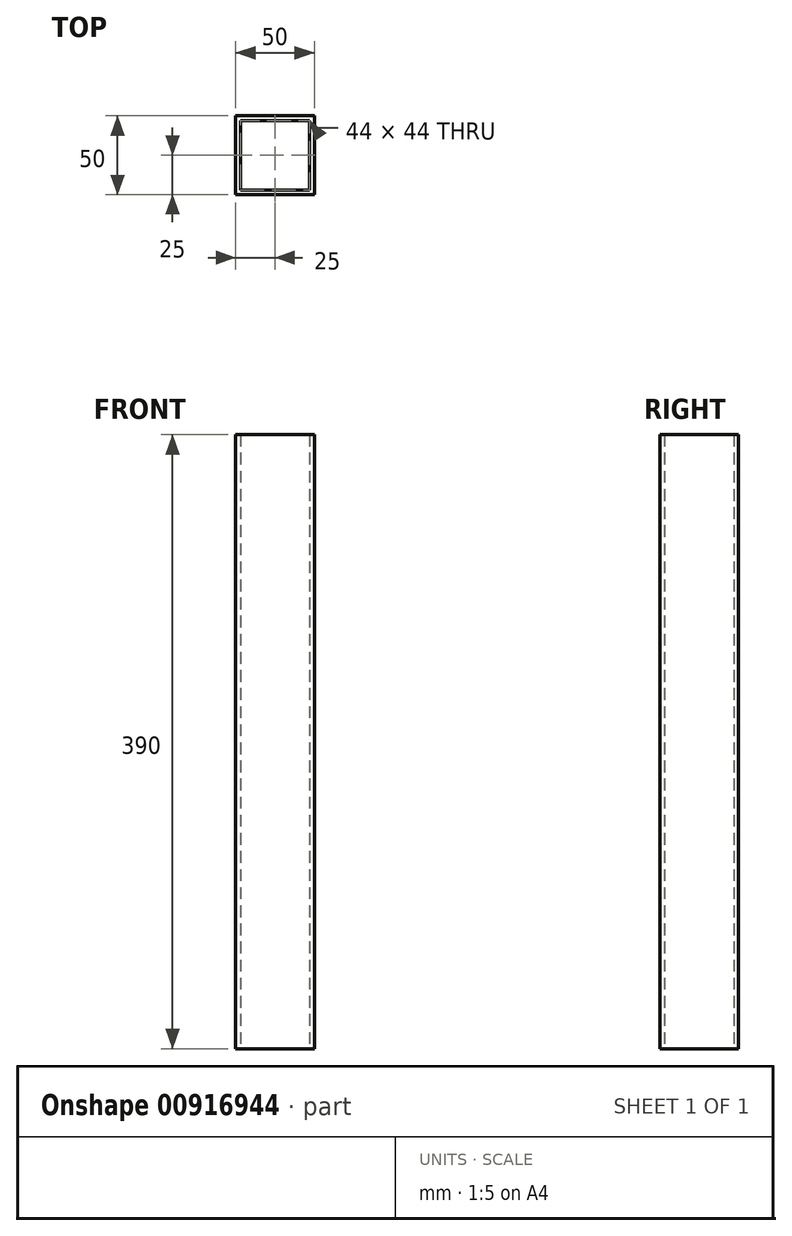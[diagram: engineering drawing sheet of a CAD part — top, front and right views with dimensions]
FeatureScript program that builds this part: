
annotation { "Feature Type Name" : "Feature", "Feature Type Description" : "" }
export const myFeature = defineFeature(function(context is Context, id is Id, definition is map)
    precondition{}
    {
        {
            var Q0;
            Q0=qCreatedBy(makeId("Top.planeOp"),FACE);
            var sketch = newSketch(context, id + "F0", { "sketchPlane" : qUnion([Q0])});
            skLineSegment(sketch, "E0.bottom", {"start": v(0, 0) * mm, "end": v(50, 0) * mm});
            skLineSegment(sketch, "E0.top", {"start": v(0, 50) * mm, "end": v(50, 50) * mm});
            skLineSegment(sketch, "E0.left", {"start": v(0, 0) * mm, "end": v(0, 50) * mm});
            skLineSegment(sketch, "E0.right", {"start": v(50, 0) * mm, "end": v(50, 50) * mm});
            skLineSegment(sketch, "E1.0", {"start": v(3, 3) * mm, "end": v(47, 3) * mm});
            skLineSegment(sketch, "E1.1", {"start": v(3, 3) * mm, "end": v(3, 47) * mm});
            skLineSegment(sketch, "E1.2", {"start": v(3, 47) * mm, "end": v(47, 47) * mm});
            skLineSegment(sketch, "E1.3", {"start": v(47, 3) * mm, "end": v(47, 47) * mm});
            skSolve(sketch);
        }
        {
            var Q0;
            Q0=makeQuery(id+"F0.imprint","IMPRINT",FACE,{"disambiguationData":[TD([[makeQuery(id+"F0.imprint","IMPRINT",EDGE,{"derivedFrom":sQuery(id+"F0.wireOp",EDGE,"E0.bottom")}),1.0]])]});
            extrude(context, id + "F1", {"entities" : qUnion([Q0]), "depth" : 390 * mm, "offsetDistance" : 25 * mm});
        }
    });
